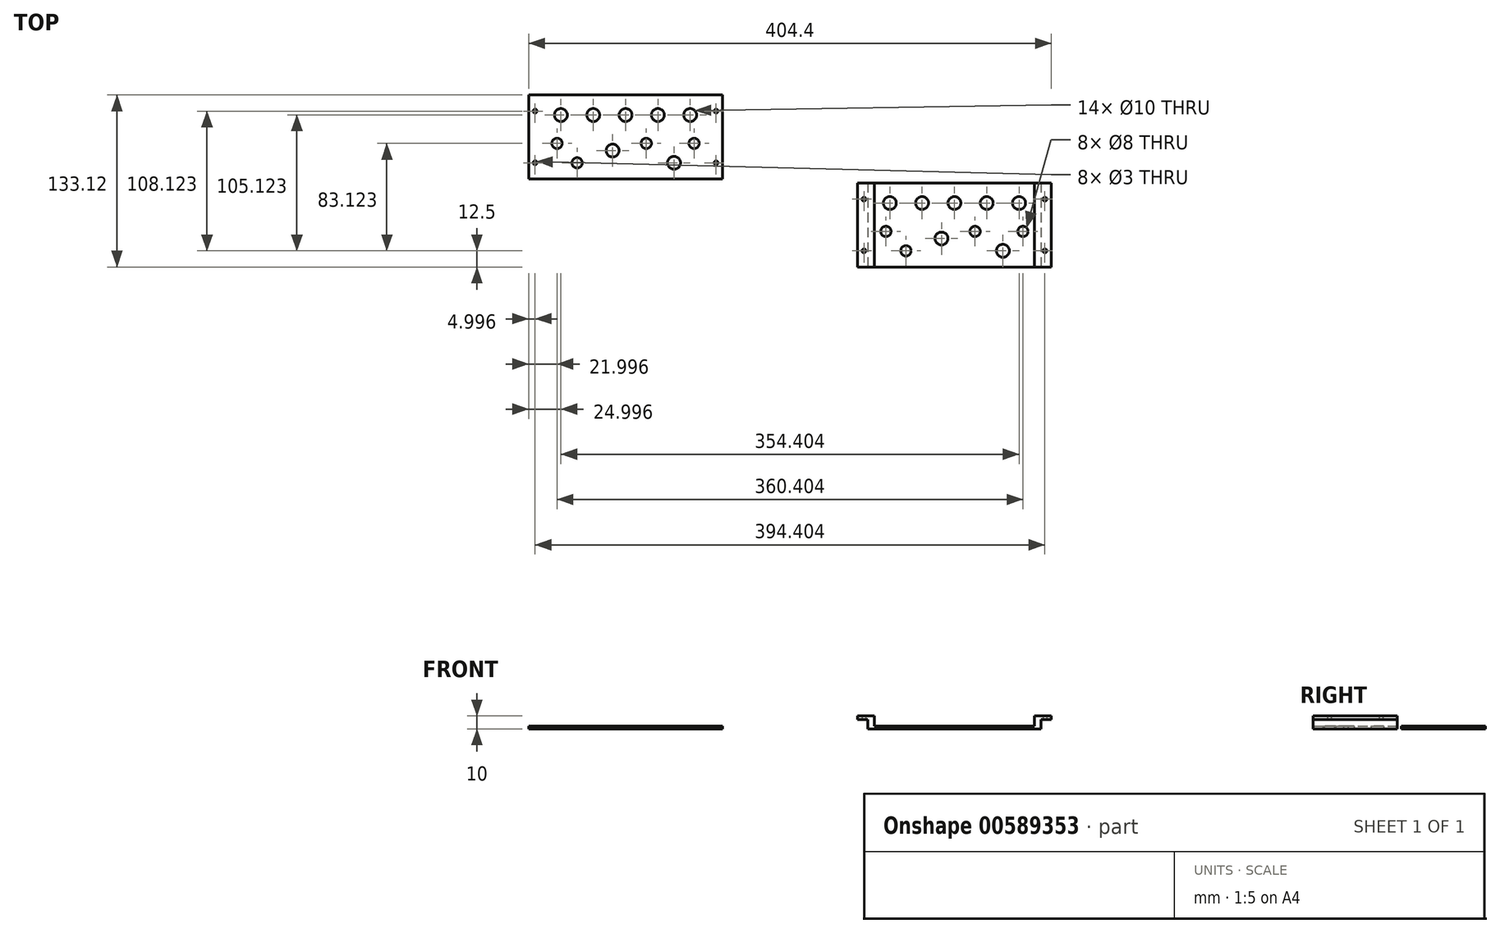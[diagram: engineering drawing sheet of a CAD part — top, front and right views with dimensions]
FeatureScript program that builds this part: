
annotation { "Feature Type Name" : "Feature", "Feature Type Description" : "" }
export const myFeature = defineFeature(function(context is Context, id is Id, definition is map)
    precondition{}
    {
        {
            var Q0;
            Q0=qCreatedBy(makeId("Top.planeOp"),FACE);
            var sketch = newSketch(context, id + "F0", { "sketchPlane" : qUnion([Q0])});
            skLineSegment(sketch, "E0.bottom", {"start": v(75, -32.5) * mm, "end": v(-75, -32.5) * mm});
            skLineSegment(sketch, "E0.top", {"start": v(75, 32.5) * mm, "end": v(-75, 32.5) * mm});
            skLineSegment(sketch, "E0.left", {"start": v(75, -32.5) * mm, "end": v(75, 32.5) * mm});
            skLineSegment(sketch, "E0.right", {"start": v(-75, -32.5) * mm, "end": v(-75, 32.5) * mm});
            skPoint(sketch, "E0.middle", {"position": v(0, 0) * mm});
            skLineSegment(sketch, "E1.bottom", {"start": v(-75, 32.5) * mm, "end": v(-65, 32.5) * mm, "construction": true});
            skLineSegment(sketch, "E1.top", {"start": v(-75, -32.5) * mm, "end": v(-65, -32.5) * mm, "construction": true});
            skLineSegment(sketch, "E1.left", {"start": v(-75, 32.5) * mm, "end": v(-75, -32.5) * mm, "construction": true});
            skLineSegment(sketch, "E1.right", {"start": v(-65, 32.5) * mm, "end": v(-65, -32.5) * mm, "construction": true});
            skLineSegment(sketch, "E2.bottom", {"start": v(75, 32.5) * mm, "end": v(65, 32.5) * mm, "construction": true});
            skLineSegment(sketch, "E2.top", {"start": v(75, -32.5) * mm, "end": v(65, -32.5) * mm, "construction": true});
            skLineSegment(sketch, "E2.left", {"start": v(75, 32.5) * mm, "end": v(75, -32.5) * mm, "construction": true});
            skLineSegment(sketch, "E2.right", {"start": v(65, 32.5) * mm, "end": v(65, -32.5) * mm, "construction": true});
            skCircle(sketch, "E3", {"center": v(-53, -5) * mm, "radius": 4 * mm});
            skCircle(sketch, "E4", {"center": v(-50, 17) * mm, "radius": 5 * mm});
            skCircle(sketch, "E5.1.0.0", {"center": v(-25, 17) * mm, "radius": 5 * mm});
            skCircle(sketch, "E5.2.0.0", {"center": v(0, 17) * mm, "radius": 5 * mm});
            skCircle(sketch, "E5.3.0.0", {"center": v(25, 17) * mm, "radius": 5 * mm});
            skCircle(sketch, "E5.4.0.0", {"center": v(50, 17) * mm, "radius": 5 * mm});
            skLineSegment(sketch, "E5.direction1", {"start": v(-50, 17) * mm, "end": v(-25, 17) * mm, "construction": true});
            skCircle(sketch, "E6", {"center": v(-53, -5) * mm, "radius": 3 * mm, "construction": true});
            skCircle(sketch, "E7", {"center": v(-37.5, -20) * mm, "radius": 4 * mm});
            skCircle(sketch, "E8", {"center": v(-37.5, -20) * mm, "radius": 3 * mm, "construction": true});
            skCircle(sketch, "E9", {"center": v(16, -5) * mm, "radius": 4 * mm});
            skCircle(sketch, "E10", {"center": v(16, -5) * mm, "radius": 3 * mm, "construction": true});
            skCircle(sketch, "E11", {"center": v(53, -5) * mm, "radius": 4 * mm});
            skCircle(sketch, "E12", {"center": v(53, -5) * mm, "radius": 3 * mm, "construction": true});
            skCircle(sketch, "E13", {"center": v(-10, -10.5) * mm, "radius": 5 * mm});
            skCircle(sketch, "E14", {"center": v(37.5, -20) * mm, "radius": 5 * mm});
            skLineSegment(sketch, "E15.bottom", {"start": v(-5, -19.5) * mm, "end": v(-15, -19.5) * mm, "construction": true});
            skLineSegment(sketch, "E15.top", {"start": v(-5, -1.5) * mm, "end": v(-15, -1.5) * mm, "construction": true});
            skLineSegment(sketch, "E15.left", {"start": v(-5, -19.5) * mm, "end": v(-5, -1.5) * mm, "construction": true});
            skLineSegment(sketch, "E15.right", {"start": v(-15, -19.5) * mm, "end": v(-15, -1.5) * mm, "construction": true});
            skCircle(sketch, "E16", {"center": v(-70, 20) * mm, "radius": 1.5 * mm});
            skCircle(sketch, "E17", {"center": v(-70, -20) * mm, "radius": 1.5 * mm});
            skCircle(sketch, "E18", {"center": v(70, 20) * mm, "radius": 1.5 * mm});
            skCircle(sketch, "E19", {"center": v(70, -20) * mm, "radius": 1.5 * mm});
            skSolve(sketch);
        }
        {
            var Q0;
            Q0=makeQuery(id+"F0.imprint","IMPRINT",FACE,{"disambiguationData":[TD([[makeQuery(id+"F0.imprint","IMPRINT",EDGE,{"derivedFrom":sQuery(id+"F0.wireOp",EDGE,"E0.bottom")}),-1.0]])]});
            extrude(context, id + "F1", {"entities" : qUnion([Q0]), "depth" : 10 * mm});
        }
        {
            var Q0;
            Q0=qCreatedBy(makeId("Top.planeOp"),FACE);
            var sketch = newSketch(context, id + "F2", { "sketchPlane" : qUnion([Q0])});
            skLineSegment(sketch, "E20.bottom", {"start": v(-179.4, 35.62) * mm, "end": v(-329.4, 35.62) * mm});
            skLineSegment(sketch, "E20.top", {"start": v(-179.4, 100.62) * mm, "end": v(-329.4, 100.62) * mm});
            skLineSegment(sketch, "E20.left", {"start": v(-179.4, 35.62) * mm, "end": v(-179.4, 100.62) * mm});
            skLineSegment(sketch, "E20.right", {"start": v(-329.4, 35.62) * mm, "end": v(-329.4, 100.62) * mm});
            skPoint(sketch, "E20.middle", {"position": v(-254.4, 68.12) * mm});
            skLineSegment(sketch, "E21.bottom", {"start": v(-329.4, 100.62) * mm, "end": v(-319.4, 100.62) * mm, "construction": true});
            skLineSegment(sketch, "E21.top", {"start": v(-329.4, 35.62) * mm, "end": v(-319.4, 35.62) * mm, "construction": true});
            skLineSegment(sketch, "E21.left", {"start": v(-329.4, 100.62) * mm, "end": v(-329.4, 35.62) * mm, "construction": true});
            skLineSegment(sketch, "E21.right", {"start": v(-319.4, 100.62) * mm, "end": v(-319.4, 35.62) * mm, "construction": true});
            skLineSegment(sketch, "E22.bottom", {"start": v(-179.4, 100.62) * mm, "end": v(-189.4, 100.62) * mm, "construction": true});
            skLineSegment(sketch, "E22.top", {"start": v(-179.4, 35.62) * mm, "end": v(-189.4, 35.62) * mm, "construction": true});
            skLineSegment(sketch, "E22.left", {"start": v(-179.4, 100.62) * mm, "end": v(-179.4, 35.62) * mm, "construction": true});
            skLineSegment(sketch, "E22.right", {"start": v(-189.4, 100.62) * mm, "end": v(-189.4, 35.62) * mm, "construction": true});
            skCircle(sketch, "E23", {"center": v(-307.4, 63.12) * mm, "radius": 4 * mm});
            skCircle(sketch, "E24", {"center": v(-304.4, 85.12) * mm, "radius": 5 * mm});
            skCircle(sketch, "E25.1.0.0", {"center": v(-279.4, 85.12) * mm, "radius": 5 * mm});
            skCircle(sketch, "E25.2.0.0", {"center": v(-254.4, 85.12) * mm, "radius": 5 * mm});
            skCircle(sketch, "E25.3.0.0", {"center": v(-229.4, 85.12) * mm, "radius": 5 * mm});
            skCircle(sketch, "E25.4.0.0", {"center": v(-204.4, 85.12) * mm, "radius": 5 * mm});
            skLineSegment(sketch, "E25.direction1", {"start": v(-304.4, 85.12) * mm, "end": v(-279.4, 85.12) * mm, "construction": true});
            skCircle(sketch, "E26", {"center": v(-307.4, 63.12) * mm, "radius": 3 * mm, "construction": true});
            skCircle(sketch, "E27", {"center": v(-291.9, 48.12) * mm, "radius": 4 * mm});
            skCircle(sketch, "E28", {"center": v(-291.9, 48.12) * mm, "radius": 3 * mm, "construction": true});
            skCircle(sketch, "E29", {"center": v(-238.4, 63.12) * mm, "radius": 4 * mm});
            skCircle(sketch, "E30", {"center": v(-238.4, 63.12) * mm, "radius": 3 * mm, "construction": true});
            skCircle(sketch, "E31", {"center": v(-201.4, 63.12) * mm, "radius": 4 * mm});
            skCircle(sketch, "E32", {"center": v(-201.4, 63.12) * mm, "radius": 3 * mm, "construction": true});
            skCircle(sketch, "E33", {"center": v(-264.4, 57.62) * mm, "radius": 5 * mm});
            skCircle(sketch, "E34", {"center": v(-216.9, 48.12) * mm, "radius": 5 * mm});
            skLineSegment(sketch, "E35.bottom", {"start": v(-259.4, 48.62) * mm, "end": v(-269.4, 48.62) * mm, "construction": true});
            skLineSegment(sketch, "E35.top", {"start": v(-259.4, 66.62) * mm, "end": v(-269.4, 66.62) * mm, "construction": true});
            skLineSegment(sketch, "E35.left", {"start": v(-259.4, 48.62) * mm, "end": v(-259.4, 66.62) * mm, "construction": true});
            skLineSegment(sketch, "E35.right", {"start": v(-269.4, 48.62) * mm, "end": v(-269.4, 66.62) * mm, "construction": true});
            skCircle(sketch, "E36", {"center": v(-324.4, 88.12) * mm, "radius": 1.5 * mm});
            skCircle(sketch, "E37", {"center": v(-324.4, 48.12) * mm, "radius": 1.5 * mm});
            skCircle(sketch, "E38", {"center": v(-184.4, 88.12) * mm, "radius": 1.5 * mm});
            skCircle(sketch, "E39", {"center": v(-184.4, 48.12) * mm, "radius": 1.5 * mm});
            skSolve(sketch);
        }
        {
            var Q0;
            Q0=makeQuery(id+"F2.imprint","IMPRINT",FACE,{"disambiguationData":[TD([[makeQuery(id+"F2.imprint","IMPRINT",EDGE,{"derivedFrom":sQuery(id+"F2.wireOp",EDGE,"E20.bottom")}),-1.0]])]});
            extrude(context, id + "F3", {"entities" : qUnion([Q0]), "depth" : 2 * mm});
        }
        {
            var Q0;
            Q0=makeQuery(id+"F1.opExtrude","SWEPT_FACE",FACE,{"disambiguationData":[OSD([sQuery(id+"F0.wireOp",EDGE,"E0.bottom")])]});
            var sketch = newSketch(context, id + "F4", { "sketchPlane" : qUnion([Q0])});
            skLineSegment(sketch, "E40.bottom", {"start": v(-75, 0) * mm, "end": v(-67, 0) * mm});
            skLineSegment(sketch, "E40.top", {"start": v(-75, 7) * mm, "end": v(-67, 7) * mm});
            skLineSegment(sketch, "E40.left", {"start": v(-75, 0) * mm, "end": v(-75, 7) * mm});
            skLineSegment(sketch, "E40.right", {"start": v(-67, 0) * mm, "end": v(-67, 7) * mm});
            skLineSegment(sketch, "E41.bottom", {"start": v(75, 0) * mm, "end": v(67, 0) * mm});
            skLineSegment(sketch, "E41.top", {"start": v(75, 7) * mm, "end": v(67, 7) * mm});
            skLineSegment(sketch, "E41.left", {"start": v(75, 0) * mm, "end": v(75, 7) * mm});
            skLineSegment(sketch, "E41.right", {"start": v(67, 0) * mm, "end": v(67, 7) * mm});
            skSolve(sketch);
        }
        {
            var Q0;
            Q0=qSketchRegion(id+"F4",true);
            extrude(context, id + "F5", {"entities" : qUnion([Q0]), "operationType" : NewBodyOperationType.REMOVE, "oppositeDirection" : true, "depth" : 70 * mm});
        }
        {
            var Q0;
            Q0=makeQuery(id+"F1.opExtrude","CAP_FACE",FACE,{"disambiguationData":[OSD([sQuery(id+"F0.wireOp",EDGE,"E0.bottom"),sQuery(id+"F0.wireOp",EDGE,"E0.top"),sQuery(id+"F0.wireOp",EDGE,"E0.left"),sQuery(id+"F0.wireOp",EDGE,"E0.right"),sQuery(id+"F0.wireOp",EDGE,"E3"),sQuery(id+"F0.wireOp",EDGE,"E4"),sQuery(id+"F0.wireOp",EDGE,"E5.1.0.0"),sQuery(id+"F0.wireOp",EDGE,"E5.2.0.0"),sQuery(id+"F0.wireOp",EDGE,"E5.3.0.0"),sQuery(id+"F0.wireOp",EDGE,"E5.4.0.0"),sQuery(id+"F0.wireOp",EDGE,"E7"),sQuery(id+"F0.wireOp",EDGE,"E9"),sQuery(id+"F0.wireOp",EDGE,"E11"),sQuery(id+"F0.wireOp",EDGE,"E13"),sQuery(id+"F0.wireOp",EDGE,"E14"),sQuery(id+"F0.wireOp",EDGE,"E16"),sQuery(id+"F0.wireOp",EDGE,"E17"),sQuery(id+"F0.wireOp",EDGE,"E18"),sQuery(id+"F0.wireOp",EDGE,"E19")])],"isStart":false});
            var sketch = newSketch(context, id + "F6", { "sketchPlane" : qUnion([Q0])});
            skLineSegment(sketch, "E42.bottom", {"start": v(62, -32.5) * mm, "end": v(-62, -32.5) * mm});
            skLineSegment(sketch, "E42.top", {"start": v(62, 32.5) * mm, "end": v(-62, 32.5) * mm});
            skLineSegment(sketch, "E42.left", {"start": v(62, -32.5) * mm, "end": v(62, 32.5) * mm});
            skLineSegment(sketch, "E42.right", {"start": v(-62, -32.5) * mm, "end": v(-62, 32.5) * mm});
            skPoint(sketch, "E42.middle", {"position": v(0, 0) * mm});
            skSolve(sketch);
        }
        {
            var Q0;
            Q0=qSketchRegion(id+"F6",true);
            extrude(context, id + "F7", {"entities" : qUnion([Q0]), "operationType" : NewBodyOperationType.REMOVE, "oppositeDirection" : true, "depth" : 8 * mm});
        }
    });
